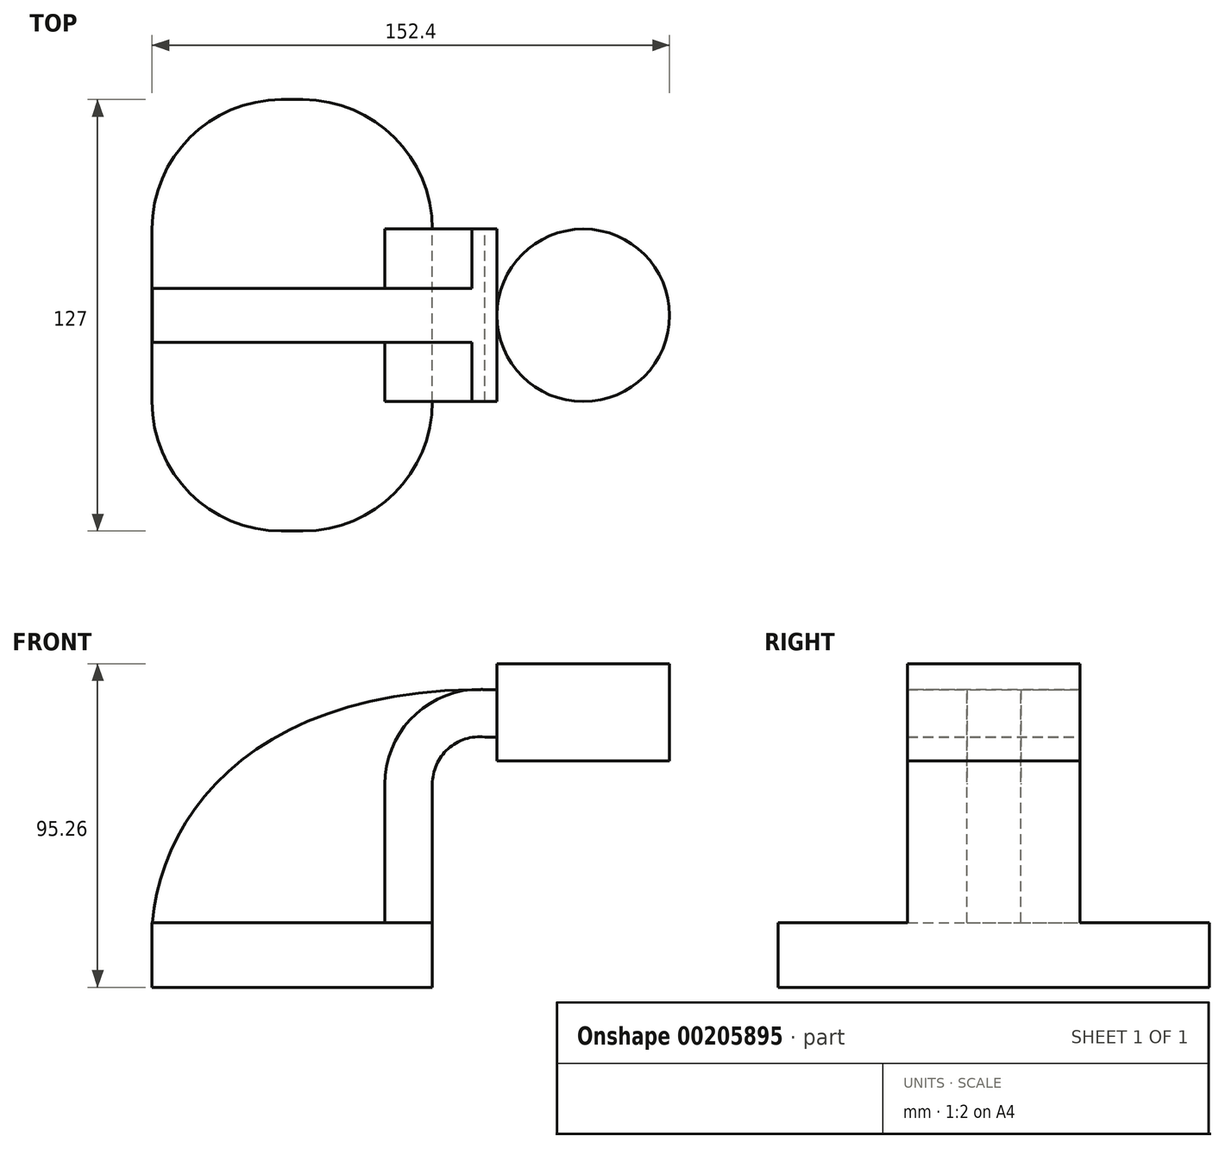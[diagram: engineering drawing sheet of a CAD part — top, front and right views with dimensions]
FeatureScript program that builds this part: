
annotation { "Feature Type Name" : "Feature", "Feature Type Description" : "" }
export const myFeature = defineFeature(function(context is Context, id is Id, definition is map)
    precondition{}
    {
        {
            var Q0;
            Q0=qCreatedBy(makeId("Front.planeOp"),FACE);
            var sketch = newSketch(context, id + "F0", { "sketchPlane" : qUnion([Q0])});
            skLineSegment(sketch, "E0.bottom", {"start": v(-41.28, 9.52) * mm, "end": v(41.28, 9.52) * mm});
            skLineSegment(sketch, "E0.top", {"start": v(-41.28, -9.53) * mm, "end": v(41.28, -9.53) * mm});
            skLineSegment(sketch, "E0.left", {"start": v(-41.28, 9.52) * mm, "end": v(-41.28, -9.53) * mm});
            skLineSegment(sketch, "E0.right", {"start": v(41.28, 9.52) * mm, "end": v(41.28, -9.53) * mm});
            skPoint(sketch, "E0.middle", {"position": v(0, 0) * mm});
            skLineSegment(sketch, "E1.bottom", {"start": v(60.33, 85.72) * mm, "end": v(111.12, 85.72) * mm});
            skLineSegment(sketch, "E1.top", {"start": v(60.33, 57.15) * mm, "end": v(111.12, 57.15) * mm});
            skLineSegment(sketch, "E1.left", {"start": v(60.33, 85.73) * mm, "end": v(60.33, 57.15) * mm});
            skLineSegment(sketch, "E1.right", {"start": v(111.13, 85.73) * mm, "end": v(111.13, 57.15) * mm});
            skPoint(sketch, "E1.middle", {"position": v(85.73, 71.44) * mm});
            skLineSegment(sketch, "E2", {"start": v(41.28, 9.52) * mm, "end": v(41.28, 50.24) * mm});
            skArc(sketch, "E3", {"start": v(56.74, 64.13) * mm, "mid": v(45.9, 60.64) * mm, "end": v(41.28, 50.24) * mm});
            skLineSegment(sketch, "E4", {"start": v(56.74, 64.13) * mm, "end": v(85.73, 64.13) * mm});
            skLineSegment(sketch, "E5", {"start": v(85.73, 64.13) * mm, "end": v(85.73, 71.44) * mm});
            skPoint(sketch, "E6", {"position": v(85.73, 57.15) * mm});
            skLineSegment(sketch, "E7.0", {"start": v(41.27, 9.52) * mm, "end": v(41.27, 50.37) * mm});
            skLineSegment(sketch, "E8.0", {"start": v(57.36, 78.1) * mm, "end": v(85.73, 78.1) * mm});
            skArc(sketch, "E8.1", {"start": v(57.36, 78.1) * mm, "mid": v(36.25, 70.73) * mm, "end": v(27.3, 50.24) * mm});
            skLineSegment(sketch, "E8.2", {"start": v(27.3, 9.52) * mm, "end": v(27.3, 50.24) * mm});
            skLineSegment(sketch, "E9", {"start": v(85.73, 57.15) * mm, "end": v(85.73, 85.72) * mm});
            skFitSpline(sketch, "E10", {"points": [v(-41.16, 9.4) * mm, v(57.36, 78.1) * mm], "startDerivative": vector(8, 99.9) * mm, "endDerivative": vector(199.82, -1.74) * mm});
            skSolve(sketch);
        }
        {
            var Q0;
            Q0=makeQuery(id+"F0.imprint","IMPRINT",FACE,{"disambiguationData":[TD([[makeQuery(id+"F0.imprint","IMPRINT",EDGE,{"derivedFrom":sQuery(id+"F0.wireOp",EDGE,"E0.top")}),1.0]])]});
            extrude(context, id + "F1", {"entities" : qUnion([Q0]), "endBound" : BoundingType.SYMMETRIC, "depth" : 127 * mm});
        }
        {
            var Q0;
            {var subQ1=sQuery(id+"F0.wireOp",EDGE,"E3");Q0=makeQuery(id+"F0.imprint","IMPRINT",FACE,{"disambiguationData":[TD([[makeQuery(id+"F0.imprint","IMPRINT",EDGE,{"derivedFrom":subQ1}),-1.0]])]});}
            var Q1;
            {var subQ0=sQuery(id+"F0.wireOp",EDGE,"E9");var subQ8=makeQuery(id+"F0.imprint","IMPRINT",VERTEX,{"derivedFrom":subQ0});Q1=makeQuery(id+"F0.imprint","IMPRINT",FACE,{"disambiguationData":[TD([[makeQuery(id+"F0.imprint","IMPRINT",EDGE,{"disambiguationData":[TD([[subQ8,1.0]])],"derivedFrom":subQ0}),1.0]])]});}
            extrude(context, id + "F2", {"entities" : qUnion([Q0, Q1]), "operationType" : NewBodyOperationType.ADD, "endBound" : BoundingType.SYMMETRIC, "depth" : 50.8 * mm});
        }
        {
            var Q0;
            {var subQ0=sQuery(id+"F0.wireOp",EDGE,"E8.2");Q0=makeQuery(id+"F0.imprint","IMPRINT",FACE,{"disambiguationData":[TD([[makeQuery(id+"F0.imprint","IMPRINT",EDGE,{"derivedFrom":subQ0}),1.0]])]});}
            extrude(context, id + "F3", {"entities" : qUnion([Q0]), "operationType" : NewBodyOperationType.ADD, "endBound" : BoundingType.SYMMETRIC, "depth" : 15.88 * mm});
        }
        {
            var Q0;
            {var subQ4=sQuery(id+"F0.wireOp",EDGE,"E1.right");Q0=makeQuery(id+"F0.imprint","IMPRINT",FACE,{"disambiguationData":[TD([[makeQuery(id+"F0.imprint","IMPRINT",EDGE,{"derivedFrom":subQ4}),-1.0]])]});}
            var Q1;
            Q1=sQuery(id+"F0.wireOp",EDGE,"E9");
            revolve(context, id + "F4", {"operationType" : NewBodyOperationType.ADD, "entities" : qUnion([Q0]), "axis" : qUnion([Q1]), "revolveType" : RevolveType.FULL});
        }
        {
            var Q0;
            Q0=makeQuery(id+"F1.opExtrude","CAP_EDGE",EDGE,{"disambiguationData":[OSD([sQuery(id+"F0.wireOp",EDGE,"E0.left")])],"isStart":false});
            var Q1;
            Q1=makeQuery(id+"F1.opExtrude","CAP_EDGE",EDGE,{"disambiguationData":[OSD([sQuery(id+"F0.wireOp",EDGE,"E0.right")])],"isStart":false});
            var Q2;
            Q2=makeQuery(id+"F1.opExtrude","CAP_EDGE",EDGE,{"disambiguationData":[OSD([sQuery(id+"F0.wireOp",EDGE,"E0.right")])],"isStart":true});
            var Q3;
            Q3=makeQuery(id+"F1.opExtrude","CAP_EDGE",EDGE,{"disambiguationData":[OSD([sQuery(id+"F0.wireOp",EDGE,"E0.left")])],"isStart":true});
            fillet(context, id + "F5", {"entities" : qUnion([Q0, Q1, Q2, Q3]), "radius" : 38.1 * mm, "tangentPropagation" : true, "allowEdgeOverflow" : false});
        }
    });
